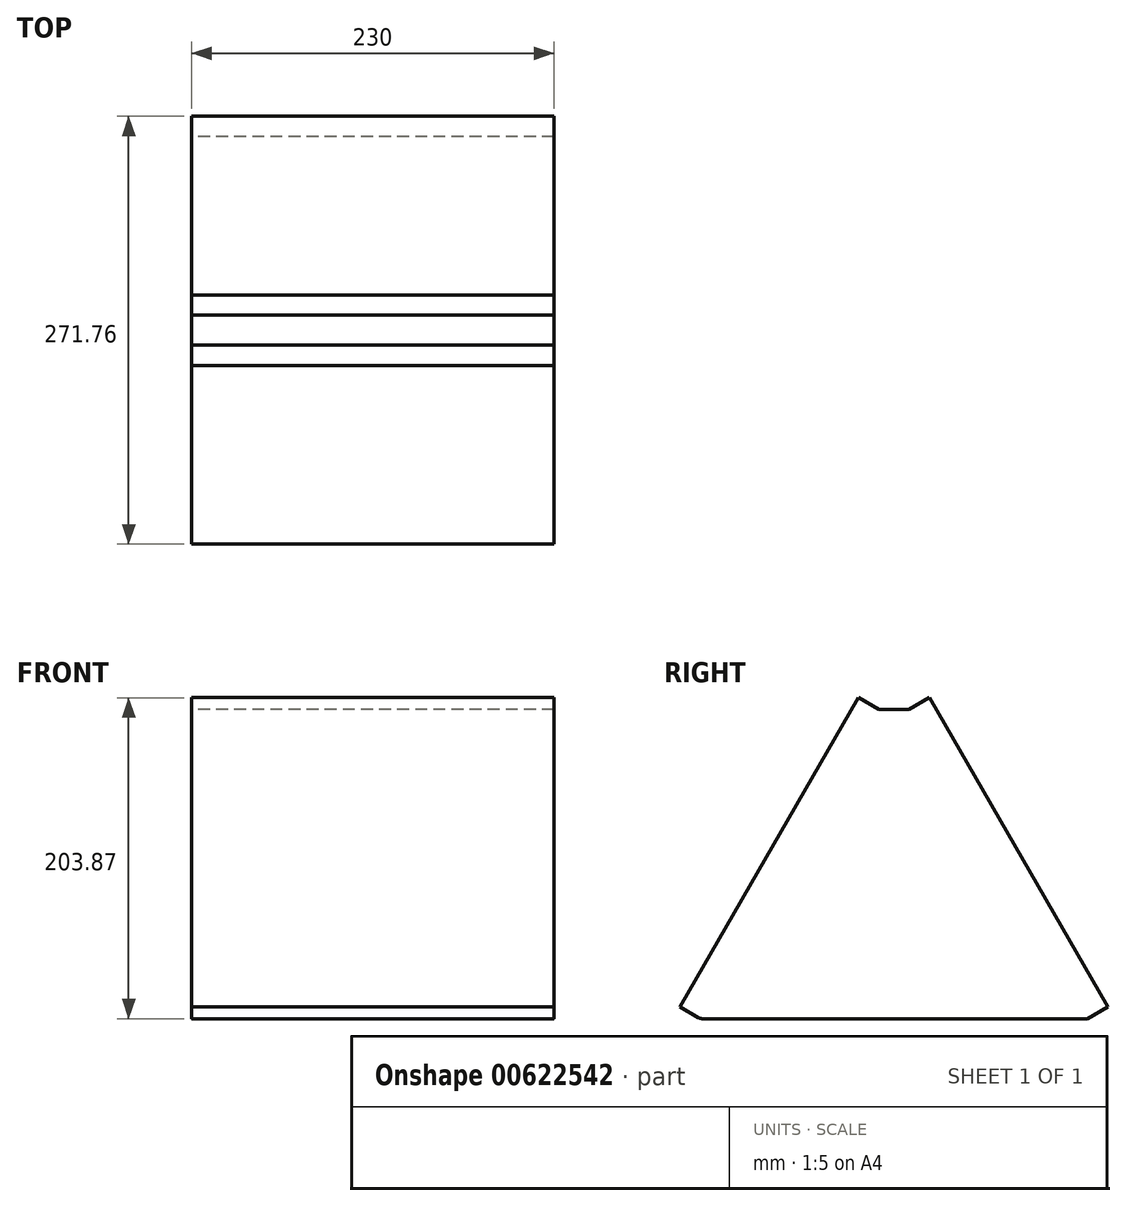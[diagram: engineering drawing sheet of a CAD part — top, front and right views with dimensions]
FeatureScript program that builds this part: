
annotation { "Feature Type Name" : "Feature", "Feature Type Description" : "" }
export const myFeature = defineFeature(function(context is Context, id is Id, definition is map)
    precondition{}
    {
        {
            var Q0;
            Q0=qCreatedBy(makeId("Right.planeOp"),FACE);
            var sketch = newSketch(context, id + "F0", { "sketchPlane" : qUnion([Q0])});
            skLineSegment(sketch, "E0.bottom", {"start": v(2.83, -129.47) * mm, "end": v(122.88, -129.47) * mm});
            skLineSegment(sketch, "E0.top", {"start": v(0.68, 66.9) * mm, "end": v(9.5, 66.9) * mm});
            skPoint(sketch, "E0.middle", {"position": v(0, 0) * mm});
            skLineSegment(sketch, "E1", {"start": v(122.88, -129.47) * mm, "end": v(135.88, -121.97) * mm});
            skLineSegment(sketch, "E2", {"start": v(135.88, -121.97) * mm, "end": v(22.5, 74.4) * mm});
            skLineSegment(sketch, "E3", {"start": v(22.5, 74.4) * mm, "end": v(9.5, 66.9) * mm});
            skLineSegment(sketch, "E4.MirrorCS", {"start": v(-135.88, -121.97) * mm, "end": v(-22.5, 74.4) * mm});
            skLineSegment(sketch, "E5.MirrorCS", {"start": v(-122.88, -129.47) * mm, "end": v(-135.87, -121.97) * mm});
            skLineSegment(sketch, "E6.MirrorCS", {"start": v(-22.5, 74.4) * mm, "end": v(-9.5, 66.9) * mm});
            skLineSegment(sketch, "E7.MirrorCS", {"start": v(-2.83, -129.47) * mm, "end": v(-122.88, -129.47) * mm});
            skLineSegment(sketch, "E8.MirrorCS", {"start": v(-0.68, 66.9) * mm, "end": v(-9.5, 66.9) * mm});
            skLineSegment(sketch, "E9", {"start": v(0.68, 66.9) * mm, "end": v(-0.68, 66.9) * mm});
            skLineSegment(sketch, "E10", {"start": v(2.83, -129.47) * mm, "end": v(-2.83, -129.47) * mm});
            skSolve(sketch);
        }
        {
            var Q0;
            Q0=makeQuery(id+"F0.imprint","IMPRINT",FACE,{"disambiguationData":[TD([[makeQuery(id+"F0.imprint","IMPRINT",EDGE,{"derivedFrom":sQuery(id+"F0.wireOp",EDGE,"E0.bottom")}),1.0]])]});
            extrude(context, id + "F1", {"entities" : qUnion([Q0]), "depth" : 230 * mm, "offsetDistance" : 25 * mm});
        }
        {
            var Q0;
            Q0=makeQuery(id+"F1.opExtrude","SWEPT_FACE",FACE,{"disambiguationData":[OSD([sQuery(id+"F0.wireOp",EDGE,"E0.top"),sQuery(id+"F0.wireOp",EDGE,"E8.MirrorCS"),sQuery(id+"F0.wireOp",EDGE,"E9")])]});
            var sketch = newSketch(context, id + "F2", { "sketchPlane" : qUnion([Q0])});
            skLineSegment(sketch, "E11", {"start": v(-308.5, 0) * mm, "end": v(487.14, 0) * mm, "construction": true});
            skEllipse(sketch, "E12", {"center": v(46.18, 298.13) * mm, "majorRadius": 21 * mm, "minorRadius": 10.8 * mm, "majorAxis": v(0, -1)});
            skEllipse(sketch, "E13", {"center": v(117.58, 277.37) * mm, "majorRadius": 19.91 * mm, "minorRadius": 10.8 * mm, "majorAxis": v(0, -1)});
            skEllipse(sketch, "E14", {"center": v(184.61, 258.42) * mm, "majorRadius": 20.52 * mm, "minorRadius": 10.19 * mm, "majorAxis": v(0, -1)});
            skEllipse(sketch, "E15", {"center": v(74.48, 212.77) * mm, "majorRadius": 20.64 * mm, "minorRadius": 10.93 * mm, "majorAxis": v(0, -1)});
            skEllipse(sketch, "E16", {"center": v(136.65, 189.82) * mm, "majorRadius": 20.16 * mm, "minorRadius": 10.29 * mm, "majorAxis": v(0, -1)});
            skEllipse(sketch, "E17.MirrorC", {"center": v(117.58, -277.37) * mm, "majorRadius": 19.91 * mm, "minorRadius": 10.8 * mm, "majorAxis": v(0, 1)});
            skEllipse(sketch, "E18.MirrorC", {"center": v(136.65, -189.82) * mm, "majorRadius": 20.16 * mm, "minorRadius": 10.29 * mm, "majorAxis": v(0, 1)});
            skEllipse(sketch, "E19.MirrorC", {"center": v(74.48, -212.77) * mm, "majorRadius": 20.64 * mm, "minorRadius": 10.93 * mm, "majorAxis": v(0, 1)});
            skEllipse(sketch, "E20.MirrorC", {"center": v(46.18, -298.13) * mm, "majorRadius": 21 * mm, "minorRadius": 10.8 * mm, "majorAxis": v(0, 1)});
            skEllipse(sketch, "E21.MirrorC", {"center": v(184.61, -258.42) * mm, "majorRadius": 20.52 * mm, "minorRadius": 10.19 * mm, "majorAxis": v(0, 1)});
            skSolve(sketch);
        }
        {
            var Q0;
            Q0=makeQuery(id+"F2.imprint","IMPRINT",FACE,{"disambiguationData":[TD([[makeQuery(id+"F2.imprint","IMPRINT",EDGE,{"derivedFrom":sQuery(id+"F2.wireOp",EDGE,"E15")}),1.0]])]});
            var Q1;
            Q1=makeQuery(id+"F2.imprint","IMPRINT",FACE,{"disambiguationData":[TD([[makeQuery(id+"F2.imprint","IMPRINT",EDGE,{"derivedFrom":sQuery(id+"F2.wireOp",EDGE,"E12")}),1.0]])]});
            var Q2;
            Q2=makeQuery(id+"F2.imprint","IMPRINT",FACE,{"disambiguationData":[TD([[makeQuery(id+"F2.imprint","IMPRINT",EDGE,{"derivedFrom":sQuery(id+"F2.wireOp",EDGE,"E13")}),1.0]])]});
            var Q3;
            Q3=makeQuery(id+"F2.imprint","IMPRINT",FACE,{"disambiguationData":[TD([[makeQuery(id+"F2.imprint","IMPRINT",EDGE,{"derivedFrom":sQuery(id+"F2.wireOp",EDGE,"E14")}),1.0]])]});
            var Q4;
            Q4=makeQuery(id+"F2.imprint","IMPRINT",FACE,{"disambiguationData":[TD([[makeQuery(id+"F2.imprint","IMPRINT",EDGE,{"derivedFrom":sQuery(id+"F2.wireOp",EDGE,"E16")}),1.0]])]});
            var Q5;
            Q5=makeQuery(id+"F2.imprint","IMPRINT",FACE,{"disambiguationData":[TD([[makeQuery(id+"F2.imprint","IMPRINT",EDGE,{"derivedFrom":sQuery(id+"F2.wireOp",EDGE,"E20.MirrorC")}),1.0]])]});
            var Q6;
            Q6=makeQuery(id+"F2.imprint","IMPRINT",FACE,{"disambiguationData":[TD([[makeQuery(id+"F2.imprint","IMPRINT",EDGE,{"derivedFrom":sQuery(id+"F2.wireOp",EDGE,"E19.MirrorC")}),1.0]])]});
            var Q7;
            Q7=makeQuery(id+"F2.imprint","IMPRINT",FACE,{"disambiguationData":[TD([[makeQuery(id+"F2.imprint","IMPRINT",EDGE,{"derivedFrom":sQuery(id+"F2.wireOp",EDGE,"E18.MirrorC")}),1.0]])]});
            var Q8;
            Q8=makeQuery(id+"F2.imprint","IMPRINT",FACE,{"disambiguationData":[TD([[makeQuery(id+"F2.imprint","IMPRINT",EDGE,{"derivedFrom":sQuery(id+"F2.wireOp",EDGE,"E17.MirrorC")}),1.0]])]});
            var Q9;
            Q9=makeQuery(id+"F2.imprint","IMPRINT",FACE,{"disambiguationData":[TD([[makeQuery(id+"F2.imprint","IMPRINT",EDGE,{"derivedFrom":sQuery(id+"F2.wireOp",EDGE,"E21.MirrorC")}),1.0]])]});
            extrude(context, id + "F3", {"entities" : qUnion([Q0, Q1, Q2, Q3, Q4, Q5, Q6, Q7, Q8, Q9]), "operationType" : NewBodyOperationType.REMOVE, "oppositeDirection" : true, "depth" : 25 * mm, "offsetDistance" : 25 * mm});
        }
        {
            var Q0;
            Q0=makeQuery(id+"F1.opExtrude","SWEPT_EDGE",EDGE,{"disambiguationData":[OSD([sQuery(id+"F0.wireOp",EDGE,"E5.MirrorCS"),sQuery(id+"F0.wireOp",EDGE,"E7.MirrorCS")])]});
            fillet(context, id + "F4", {"entities" : qUnion([Q0]), "radius" : 5 * mm, "tangentPropagation" : true, "allowEdgeOverflow" : false});
        }
    });
